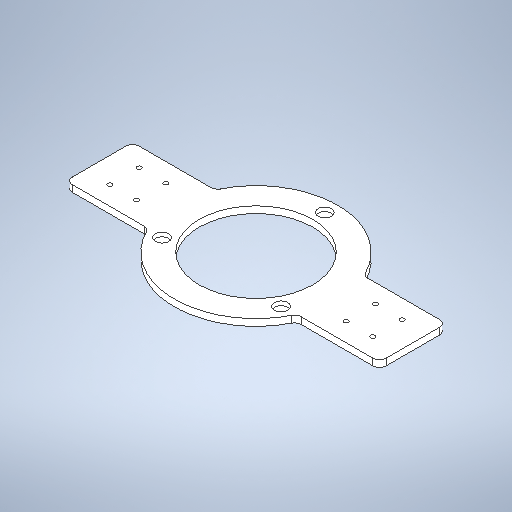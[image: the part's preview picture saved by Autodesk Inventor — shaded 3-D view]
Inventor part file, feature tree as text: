
AUTODESK INVENTOR PART (.ipt)
format: ipt  version: 2025 (Build 290162000, 162)  size: 302,592 bytes
history: native  units: in
note: dims shown in document units (in); Inventor stores cm internally (conversion verified against a paired STEP export)
features: sketch x4, hole x2, extrude x1, fillet x1
ambient origin geometry x8: Origin, YZ Plane, XZ Plane, XY Plane, X Axis, Y Axis, Z Axis, Center Point
bodies: Solid1 (feature_tree)
feature tree (8):
  extrude  "Extrusion1"  Depth=0.1969in TaperAngle=0.0deg
  hole  "Hole1"  [1 undecoded]
  fillet  "Fillet2"  Radius=9.252in
  hole  "Hole3"  [1 undecoded]
  sketch  "Sketch1"  dims[d0=3.3465in d3=0.1969in d4=0.0in]
  sketch  "Sketch2"  dims[d11=0.1276in d12=0.315in d13=0.1575in d14=0.0787in d15=90.0deg d16=0.4646in d17=0.8108in d29=2.4016in d46=9.252in]
  sketch  "Sketch4"  dims[d52=0.748in d53=0.5512in d54=0.1575in d55=0.7874in d56=0.1969in d57=4.0551in d58=1.1811in d60=360.0deg d62=0.3937in d63=0.1181in d64=0.1575in d65=0.0787in d66=90.0deg d67=0.1181in d68=0.0in]
  sketch  "Sketch Circular Pattern2"  dims[d47=1.9685in d51=0.1575in]
note: 2 required parameter values undecoded (feature->parameter linkage not recoverable at this tier; creation-order binding heuristic only, values carry confidence <= 0.55)
